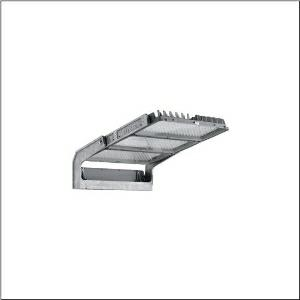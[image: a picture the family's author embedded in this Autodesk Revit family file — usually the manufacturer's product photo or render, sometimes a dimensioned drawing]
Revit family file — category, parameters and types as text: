
# Revit family: floodlight_fl_11_maxi_pro___rs08_5xa779124l01gb_5403
name_source: partatom
category: Lighting Fixtures
units: mm (PartAtom-declared; Revit-internal decimal feet)

## family parameters
Cut with Voids When Loaded = No
Host = Face
Light Source = No
Part Type = Normal
Room Calculation Point = No
Round Connector Dimension = Use Diameter
Shared = No

## types (1)
- --- (1 x LED, 121700 lm, 1227.1 W, 5700K)
    Apparent Load = 1227 VA
    CIE Flux Codes = 70 87 98 100 100
    Color Rendering = 90
    Color Temperature = 5700K
    Default Elevation = 1800 mm
    Description = Floodlight FL 11  maxi  pro floodlight; light control with lens of PMMA; cover panel of toughened safety glass, transparent; light distribution: RS08, rotationally symmetric direct distribution, LEDcolour temperature: 5700K, rated luminous flux: 121.700lm, colour rendering: CRI > 90, light colour: 957; luminous efficacy: 99lm/W; brightness control: DALI 2; with terminal, 5-pole, max. 2.5mm², mains connection: 220..240V/380..400V AC, 50/60Hz, surge voltage resistance: line to ground: 10kV, service life up to 100,000h L90. Typical operating time: 1000h per year, ECG replaceable separately, LED unit replaceable without ESD environment, dustproof LED module, dimming range 10..100%; 1227W floodlight with 3x LED unit of diecast aluminium, coated grey; length: 1.003mm / width: 651mm / height: 338mm; mounting bracket, of diecast aluminium, uncoated, natural, protection rating (complete): IP66; insulation class (complete): insulation class I (protective earthing); certification: CE, ENEC, VDE; ball protection: ball impact resistant, only for outdoor installations in the designated locations, permissible operating ambient temperature: -45..+55°C, permissible storage temperature: -40..+85°Cpackaging unit: 1 piece

Light Distribution: RS08
    Height = 320 mm
    Lamp = 1 x LED
    Lamp Light Flux = 121700 lm
    Lamp Power = 1227.1 W
    Lamp count = 1
    Length = 1002 mm
    Luminous efficacy = 99 lm/W
    Manufacturer = Siteco
    ModVariant = No
    Model = 5XA779124L01GB
    Mounting Place = Ceiling
    Mounting Type = Surface mounted
    Number of Poles = 1
    OnlyDefault = Yes
    Power Factor = 1
    Product Name = Floodlight FL 11 maxi pro | RS08
    Product group = floodlight | ceiling mounted
    ProductGroupID = 301
    Protection Class = Protection class I
    Protection Degree = IP 66
    RLX_Detail_Level = 1
    RLX_Emergency_Light_Flux = 0 lm
    RLX_Emergency_Type = 0
    RLX_Emergency_Type_DB = No
    RlxData = <blob elided: 40445 chars, md5=e4500acd>
    Socket = socket
    Standby Power = 0 W
    System Light Flux = 121700 lm
    System Power = 1227 W
    Type Comments = factory setting: luminous flux: 100 % | dim-lin: 254 | 840 mA
    Type Image = l_1356210.jpg
    URL = http://relux.com
    VarID = @adj_024928
    Voltage = 0 V
    Weight = 0.00 kg
    Width = 655 mm

## geometry (parser evidence)
native form markers: Blend x4, Sweep x11
no freeform markers — native parametric forms only
